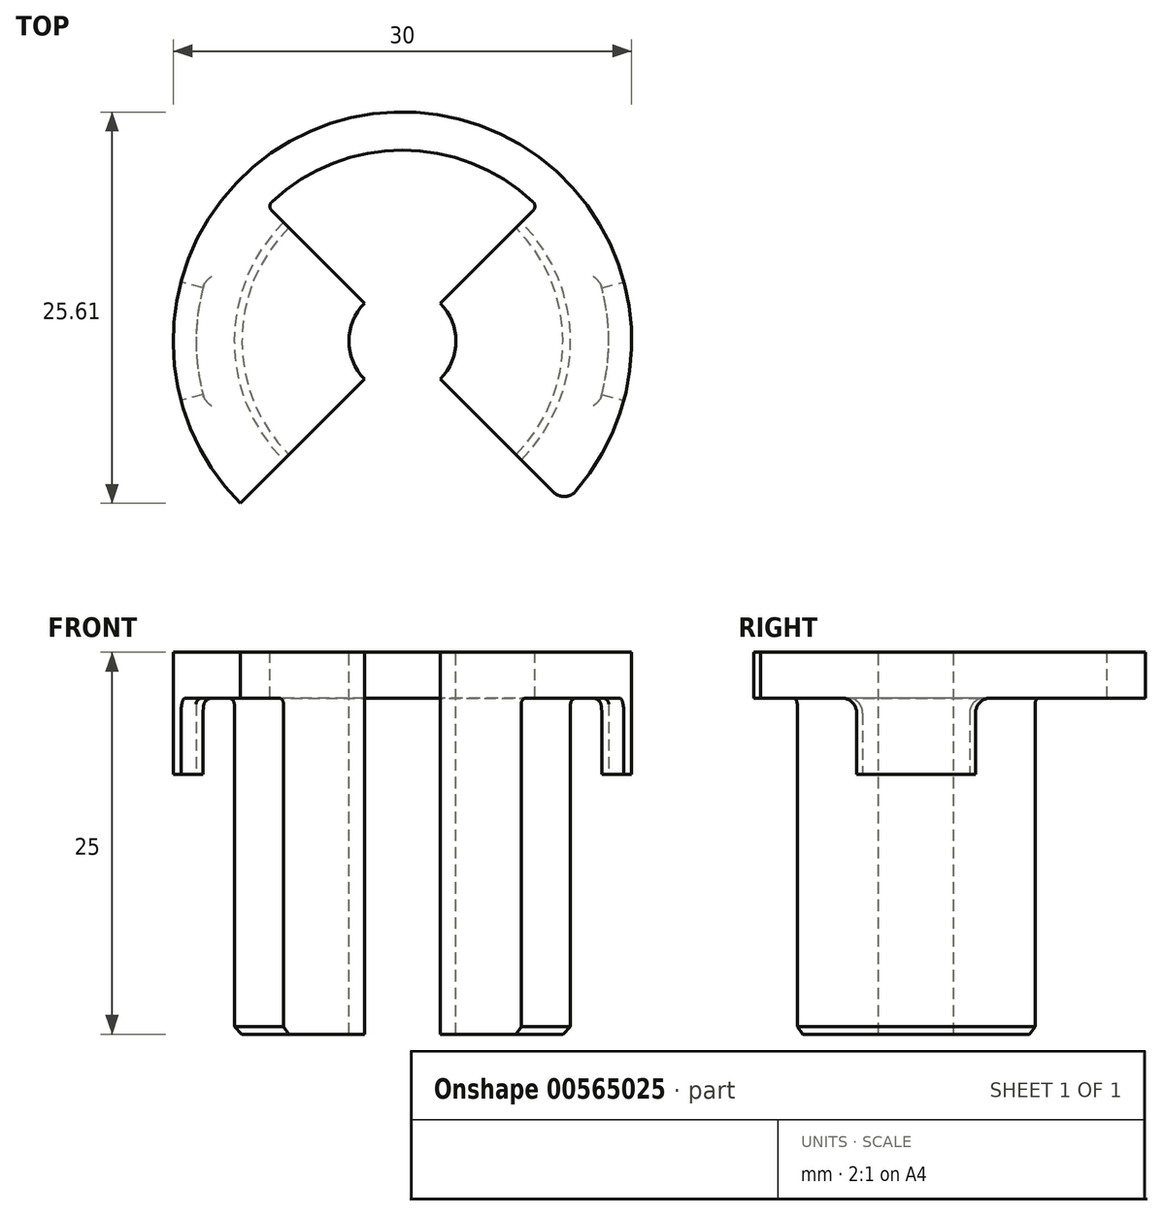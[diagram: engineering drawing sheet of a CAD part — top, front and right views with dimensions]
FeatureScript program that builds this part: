
annotation { "Feature Type Name" : "Feature", "Feature Type Description" : "" }
export const myFeature = defineFeature(function(context is Context, id is Id, definition is map)
    precondition{}
    {
        {
            var Q0;
            Q0=qCreatedBy(makeId("Top.planeOp"),FACE);
            var sketch = newSketch(context, id + "F0", { "sketchPlane" : qUnion([Q0])});
            skCircle(sketch, "E0", {"center": v(0, 0) * mm, "radius": 11 * mm});
            skCircle(sketch, "E1", {"center": v(0, 0) * mm, "radius": 3.5 * mm});
            skSolve(sketch);
        }
        {
            var Q0;
            Q0=qSketchRegion(id+"F0",true);
            extrude(context, id + "F1", {"entities" : qUnion([Q0]), "oppositeDirection" : true, "depth" : 25 * mm, "offsetDistance" : 25 * mm});
        }
        {
            var Q0;
            Q0=qCreatedBy(makeId("Top.planeOp"),FACE);
            var sketch = newSketch(context, id + "F2", { "sketchPlane" : qUnion([Q0])});
            skCircle(sketch, "E2", {"center": v(0, 0) * mm, "radius": 15 * mm});
            skCircle(sketch, "E3.0", {"center": v(0, 0) * mm, "radius": 3.5 * mm});
            skSolve(sketch);
        }
        {
            var Q0;
            Q0=qSketchRegion(id+"F2",true);
            extrude(context, id + "F3", {"entities" : qUnion([Q0]), "operationType" : NewBodyOperationType.ADD, "oppositeDirection" : true, "depth" : 8 * mm, "offsetDistance" : 25 * mm});
        }
        {
            var Q0;
            Q0=makeQuery(id+"F3.opExtrude","CAP_FACE",FACE,{"disambiguationData":[OSD([sQuery(id+"F2.wireOp",EDGE,"E2"),sQuery(id+"F2.wireOp",EDGE,"E3.0")])],"isStart":false});
            var sketch = newSketch(context, id + "F4", { "sketchPlane" : qUnion([Q0])});
            skCircle(sketch, "E4", {"center": v(0, 0) * mm, "radius": 13.5 * mm});
            skCircle(sketch, "E5.0", {"center": v(0, 0) * mm, "radius": 11 * mm});
            skSolve(sketch);
        }
        {
            var Q0;
            Q0=qSketchRegion(id+"F4",true);
            extrude(context, id + "F5", {"entities" : qUnion([Q0]), "operationType" : NewBodyOperationType.REMOVE, "oppositeDirection" : true, "depth" : 5 * mm, "offsetDistance" : 25 * mm});
        }
        {
            var Q0;
            Q0=makeQuery(id+"F5.boolean.opBoolean","COPY",EDGE,{"derivedFrom":makeQuery(id+"F5.opExtrude","CAP_EDGE",EDGE,{"disambiguationData":[OSD([sQuery(id+"F4.wireOp",EDGE,"E4")])],"isStart":false})});
            fillet(context, id + "F6", {"entities" : qUnion([Q0]), "radius" : .4 * mm, "tangentPropagation" : true, "allowEdgeOverflow" : false});
        }
        {
            var Q0;
            Q0=qCreatedBy(makeId("Top.planeOp"),FACE);
            var sketch = newSketch(context, id + "F7", { "sketchPlane" : qUnion([Q0])});
            skLineSegment(sketch, "E6", {"start": v(0, 0) * mm, "end": v(20, 0) * mm, "construction": true});
            skLineSegment(sketch, "E7", {"start": v(0, 0) * mm, "end": v(0, 21.36) * mm, "construction": true});
            skArc(sketch, "E8.0", {"start": v(2.47, 2.47) * mm, "mid": v(0, 3.5) * mm, "end": v(-2.47, 2.47) * mm});
            skLineSegment(sketch, "E9", {"start": v(0, 0) * mm, "end": v(14.8, 14.8) * mm, "construction": true});
            skArc(sketch, "E10.0", {"start": v(10.6, 10.6) * mm, "mid": v(0, 15) * mm, "end": v(-10.6, 10.6) * mm});
            skLineSegment(sketch, "E11", {"start": v(2.47, 2.47) * mm, "end": v(10.6, 10.6) * mm});
            skLineSegment(sketch, "E12.MirrorCS", {"start": v(-2.47, 2.47) * mm, "end": v(-10.6, 10.6) * mm});
            skArc(sketch, "E13.MirrorCS", {"start": v(2.47, -2.47) * mm, "mid": v(0, -3.5) * mm, "end": v(-2.47, -2.47) * mm});
            skArc(sketch, "E14.MirrorCS", {"start": v(10.6, -10.6) * mm, "mid": v(0, -15) * mm, "end": v(-10.6, -10.6) * mm});
            skLineSegment(sketch, "E15.MirrorCS", {"start": v(-2.47, -2.47) * mm, "end": v(-10.6, -10.6) * mm});
            skLineSegment(sketch, "E16.MirrorCS", {"start": v(2.47, -2.47) * mm, "end": v(10.6, -10.6) * mm});
            skSolve(sketch);
        }
        {
            var Q0;
            Q0=qSketchRegion(id+"F7",true);
            extrude(context, id + "F8", {"entities" : qUnion([Q0]), "operationType" : NewBodyOperationType.REMOVE, "oppositeDirection" : true, "depth" : 25 * mm, "offsetDistance" : 25 * mm});
        }
        {
            var Q0;
            {var subQ0=sQuery(id+"F2.wireOp",EDGE,"E2");Q0=makeQuery(id+"F8.boolean.opBoolean","SPLIT",FACE,{"disambiguationData":[TD([makeQuery(id+"F8.opExtrude","SWEPT_FACE",FACE,{"disambiguationData":[OSD([sQuery(id+"F7.wireOp",EDGE,"E11")])]})])],"derivedFrom":makeQuery(id+"F3.opExtrude","CAP_FACE",FACE,{"disambiguationData":[OSD([subQ0,sQuery(id+"F2.wireOp",EDGE,"E3.0")])],"isStart":false})});}
            var sketch = newSketch(context, id + "F9", { "sketchPlane" : qUnion([Q0])});
            skLineSegment(sketch, "E17", {"start": v(0, 0) * mm, "end": v(21.72, 0) * mm, "construction": true});
            skLineSegment(sketch, "E18", {"start": v(0, 0) * mm, "end": v(0, 13.45) * mm, "construction": true});
            skLineSegment(sketch, "E19", {"start": v(0, 0) * mm, "end": v(16.68, 4.47) * mm, "construction": true});
            skLineSegment(sketch, "E20", {"start": v(10.63, 2.85) * mm, "end": v(15.45, 4.14) * mm});
            skArc(sketch, "E21", {"start": v(10.63, 2.85) * mm, "mid": v(0, 11) * mm, "end": v(-10.63, 2.85) * mm});
            skArc(sketch, "E22", {"start": v(15.45, 4.14) * mm, "mid": v(0, 16) * mm, "end": v(-15.45, 4.14) * mm});
            skLineSegment(sketch, "E23.MirrorCS", {"start": v(-10.63, 2.85) * mm, "end": v(-15.45, 4.14) * mm});
            skLineSegment(sketch, "E24.MirrorCS", {"start": v(10.63, -2.85) * mm, "end": v(15.45, -4.14) * mm});
            skLineSegment(sketch, "E25.MirrorCS", {"start": v(-10.63, -2.85) * mm, "end": v(-15.45, -4.14) * mm});
            skArc(sketch, "E26.MirrorCS", {"start": v(10.63, -2.85) * mm, "mid": v(0, -11) * mm, "end": v(-10.63, -2.85) * mm});
            skArc(sketch, "E27.MirrorCS", {"start": v(15.45, -4.14) * mm, "mid": v(0, -16) * mm, "end": v(-15.45, -4.14) * mm});
            skSolve(sketch);
        }
        {
            var Q0;
            Q0=qSketchRegion(id+"F9",true);
            var Q1;
            {var subQ0=sQuery(id+"F4.wireOp",EDGE,"E4");var subQ1=sQuery(id+"F4.wireOp",EDGE,"E5.0");Q1=makeQuery(id+"F8.boolean.opBoolean","SPLIT",FACE,{"disambiguationData":[TD([makeQuery(id+"F8.opExtrude","SWEPT_FACE",FACE,{"disambiguationData":[OSD([sQuery(id+"F7.wireOp",EDGE,"E11")])]})])],"derivedFrom":makeQuery(id+"F5.boolean.opBoolean","COPY",FACE,{"derivedFrom":makeQuery(id+"F5.opExtrude","CAP_FACE",FACE,{"disambiguationData":[OSD([subQ0,subQ1])],"isStart":false})})});}
            extrude(context, id + "F10", {"entities" : qUnion([Q0]), "operationType" : NewBodyOperationType.REMOVE, "endBound" : BoundingType.UP_TO_SURFACE, "oppositeDirection" : true, "depth" : 25 * mm, "endBoundEntityFace" : qUnion([Q1]), "offsetDistance" : 25 * mm});
        }
        {
            var Q0;
            Q0=makeQuery(id+"F10.boolean.opBoolean","COPY",EDGE,{"derivedFrom":makeQuery(id+"F10.opExtrude","CAP_EDGE",EDGE,{"disambiguationData":[OSD([sQuery(id+"F9.wireOp",EDGE,"E25.MirrorCS")])],"isStart":false})});
            var Q1;
            Q1=makeQuery(id+"F10.boolean.opBoolean","COPY",EDGE,{"derivedFrom":makeQuery(id+"F10.opExtrude","CAP_EDGE",EDGE,{"disambiguationData":[OSD([sQuery(id+"F9.wireOp",EDGE,"E23.MirrorCS")])],"isStart":false})});
            var Q2;
            Q2=makeQuery(id+"F10.boolean.opBoolean","COPY",EDGE,{"derivedFrom":makeQuery(id+"F10.opExtrude","CAP_EDGE",EDGE,{"disambiguationData":[OSD([sQuery(id+"F9.wireOp",EDGE,"E24.MirrorCS")])],"isStart":false})});
            var Q3;
            Q3=makeQuery(id+"F10.boolean.opBoolean","COPY",EDGE,{"derivedFrom":makeQuery(id+"F10.opExtrude","CAP_EDGE",EDGE,{"disambiguationData":[OSD([sQuery(id+"F9.wireOp",EDGE,"E20")])],"isStart":false})});
            fillet(context, id + "F11", {"entities" : qUnion([Q0, Q1, Q2, Q3]), "radius" : 1 * mm, "tangentPropagation" : true, "allowEdgeOverflow" : false});
        }
        {
            var Q0;
            Q0=makeQuery(id+"F8.boolean.opBoolean","COPY",EDGE,{"derivedFrom":makeQuery(id+"F8.opExtrude","SWEPT_EDGE",EDGE,{"disambiguationData":[OSD([sQuery(id+"F7.wireOp",EDGE,"E14.MirrorCS"),sQuery(id+"F7.wireOp",EDGE,"E16.MirrorCS")])]})});
            var Q1;
            Q1=makeQuery(id+"F8.boolean.opBoolean","COPY",EDGE,{"derivedFrom":makeQuery(id+"F8.opExtrude","SWEPT_EDGE",EDGE,{"disambiguationData":[OSD([sQuery(id+"F7.wireOp",EDGE,"E10.0"),sQuery(id+"F7.wireOp",EDGE,"E11")])]})});
            var Q2;
            Q2=makeQuery(id+"F8.boolean.opBoolean","COPY",EDGE,{"derivedFrom":makeQuery(id+"F8.opExtrude","SWEPT_EDGE",EDGE,{"disambiguationData":[OSD([sQuery(id+"F7.wireOp",EDGE,"E10.0"),sQuery(id+"F7.wireOp",EDGE,"E12.MirrorCS")])]})});
            var Q3;
            Q3=makeQuery(id+"F8.boolean.opBoolean","COPY",EDGE,{"derivedFrom":makeQuery(id+"F8.opExtrude","SWEPT_EDGE",EDGE,{"disambiguationData":[OSD([sQuery(id+"F7.wireOp",EDGE,"E14.MirrorCS"),sQuery(id+"F7.wireOp",EDGE,"E15.MirrorCS")])]})});
            fillet(context, id + "F12", {"entities" : qUnion([Q0, Q1, Q2, Q3]), "radius" : 1 * mm, "tangentPropagation" : true, "allowEdgeOverflow" : false});
        }
        {
            var Q0;
            {var subQ0=sQuery(id+"F0.wireOp",EDGE,"E0");Q0=makeQuery(id+"F8.boolean.opBoolean","SPLIT",EDGE,{"disambiguationData":[TD([makeQuery(id+"F8.opExtrude","SWEPT_FACE",FACE,{"disambiguationData":[OSD([sQuery(id+"F7.wireOp",EDGE,"E12.MirrorCS")])]})])],"derivedFrom":makeQuery(id+"F1.opExtrude","CAP_EDGE",EDGE,{"disambiguationData":[OSD([subQ0])],"isStart":false})});}
            var Q1;
            {var subQ0=sQuery(id+"F0.wireOp",EDGE,"E0");Q1=makeQuery(id+"F8.boolean.opBoolean","SPLIT",EDGE,{"disambiguationData":[TD([makeQuery(id+"F8.opExtrude","SWEPT_FACE",FACE,{"disambiguationData":[OSD([sQuery(id+"F7.wireOp",EDGE,"E11")])]})])],"derivedFrom":makeQuery(id+"F1.opExtrude","CAP_EDGE",EDGE,{"disambiguationData":[OSD([subQ0])],"isStart":false})});}
            chamfer(context, id + "F13", {"entities" : qUnion([Q0, Q1]), "width" : .5 * mm, "tangentPropagation" : true});
        }
        {
            var Q0;
            Q0=qCreatedBy(makeId("Top.planeOp"),FACE);
            var sketch = newSketch(context, id + "F14", { "sketchPlane" : qUnion([Q0])});
            skLineSegment(sketch, "E28", {"start": v(12.5, 0) * mm, "end": v(17.1, 0) * mm, "construction": true});
            skLineSegment(sketch, "E29", {"start": v(0, 0) * mm, "end": v(0, 15.9) * mm, "construction": true});
            skArc(sketch, "E30", {"start": v(15, 0) * mm, "mid": v(0, 15) * mm, "end": v(-15, 0) * mm});
            skArc(sketch, "E31", {"start": v(12.5, 0) * mm, "mid": v(0, 12.5) * mm, "end": v(-12.5, 0) * mm});
            skLineSegment(sketch, "E32", {"start": v(15, 0) * mm, "end": v(12.5, 0) * mm});
            skLineSegment(sketch, "E33.trimOffspring", {"start": v(-12.5, 0) * mm, "end": v(-15, 0) * mm});
            skSolve(sketch);
        }
        {
            var Q0;
            Q0 = qSketchRegion(id + "F14", true);
            extrude(context, id + "F15", {"entities" : qUnion([Q0]), "operationType" : NewBodyOperationType.ADD, "oppositeDirection" : true, "depth" : 3 * mm, "offsetDistance" : 25 * mm});
        }
        {
            var Q0;
            {var subQ0=sQuery(id+"F4.wireOp",EDGE,"E5.0");Q0=makeQuery(id+"F8.boolean.opBoolean","SPLIT",EDGE,{"disambiguationData":[TD([makeQuery(id+"F8.opExtrude","SWEPT_FACE",FACE,{"disambiguationData":[OSD([sQuery(id+"F7.wireOp",EDGE,"E11")])]})])],"derivedFrom":makeQuery(id+"F5.boolean.opBoolean","COPY",EDGE,{"derivedFrom":makeQuery(id+"F5.opExtrude","CAP_EDGE",EDGE,{"disambiguationData":[OSD([subQ0])],"isStart":false})})});}
            var Q1;
            {var subQ0=sQuery(id+"F4.wireOp",EDGE,"E5.0");Q1=makeQuery(id+"F8.boolean.opBoolean","SPLIT",EDGE,{"disambiguationData":[TD([makeQuery(id+"F8.opExtrude","SWEPT_FACE",FACE,{"disambiguationData":[OSD([sQuery(id+"F7.wireOp",EDGE,"E12.MirrorCS")])]})])],"derivedFrom":makeQuery(id+"F5.boolean.opBoolean","COPY",EDGE,{"derivedFrom":makeQuery(id+"F5.opExtrude","CAP_EDGE",EDGE,{"disambiguationData":[OSD([subQ0])],"isStart":false})})});}
            var Q2;
            Q2=makeQuery(id+"F15.boolean.opBoolean","INTERSECT",EDGE,{"derivedFrom":[makeQuery(id+"F8.boolean.opBoolean","COPY",FACE,{"derivedFrom":makeQuery(id+"F8.opExtrude","SWEPT_FACE",FACE,{"disambiguationData":[OSD([sQuery(id+"F7.wireOp",EDGE,"E12.MirrorCS")])]})}),makeQuery(id+"F15.opExtrude","CAP_FACE",FACE,{"disambiguationData":[OSD([sQuery(id+"F14.wireOp",EDGE,"E30"),sQuery(id+"F14.wireOp",EDGE,"E31"),sQuery(id+"F14.wireOp",EDGE,"E32"),sQuery(id+"F14.wireOp",EDGE,"E33.trimOffspring")])],"isStart":false})]});
            var Q3;
            Q3=makeQuery(id+"F15.boolean.opBoolean","INTERSECT",EDGE,{"derivedFrom":[makeQuery(id+"F8.boolean.opBoolean","COPY",FACE,{"derivedFrom":makeQuery(id+"F8.opExtrude","SWEPT_FACE",FACE,{"disambiguationData":[OSD([sQuery(id+"F7.wireOp",EDGE,"E11")])]})}),makeQuery(id+"F15.opExtrude","CAP_FACE",FACE,{"disambiguationData":[OSD([sQuery(id+"F14.wireOp",EDGE,"E30"),sQuery(id+"F14.wireOp",EDGE,"E31"),sQuery(id+"F14.wireOp",EDGE,"E32"),sQuery(id+"F14.wireOp",EDGE,"E33.trimOffspring")])],"isStart":false})]});
            var Q4;
            Q4=makeQuery(id+"F15.boolean.opBoolean","INTERSECT",EDGE,{"derivedFrom":[makeQuery(id+"F8.boolean.opBoolean","COPY",FACE,{"derivedFrom":makeQuery(id+"F8.opExtrude","SWEPT_FACE",FACE,{"disambiguationData":[OSD([sQuery(id+"F7.wireOp",EDGE,"E12.MirrorCS")])]})}),makeQuery(id+"F15.opExtrude","SWEPT_FACE",FACE,{"disambiguationData":[OSD([sQuery(id+"F14.wireOp",EDGE,"E31")])]})]});
            var Q5;
            Q5=makeQuery(id+"F15.boolean.opBoolean","INTERSECT",EDGE,{"derivedFrom":[makeQuery(id+"F8.boolean.opBoolean","COPY",FACE,{"derivedFrom":makeQuery(id+"F8.opExtrude","SWEPT_FACE",FACE,{"disambiguationData":[OSD([sQuery(id+"F7.wireOp",EDGE,"E11")])]})}),makeQuery(id+"F15.opExtrude","SWEPT_FACE",FACE,{"disambiguationData":[OSD([sQuery(id+"F14.wireOp",EDGE,"E31")])]})]});
            fillet(context, id + "F16", {"entities" : qUnion([Q0, Q1, Q2, Q3, Q4, Q5]), "radius" : .4 * mm, "tangentPropagation" : true, "allowEdgeOverflow" : false});
        }
    });
